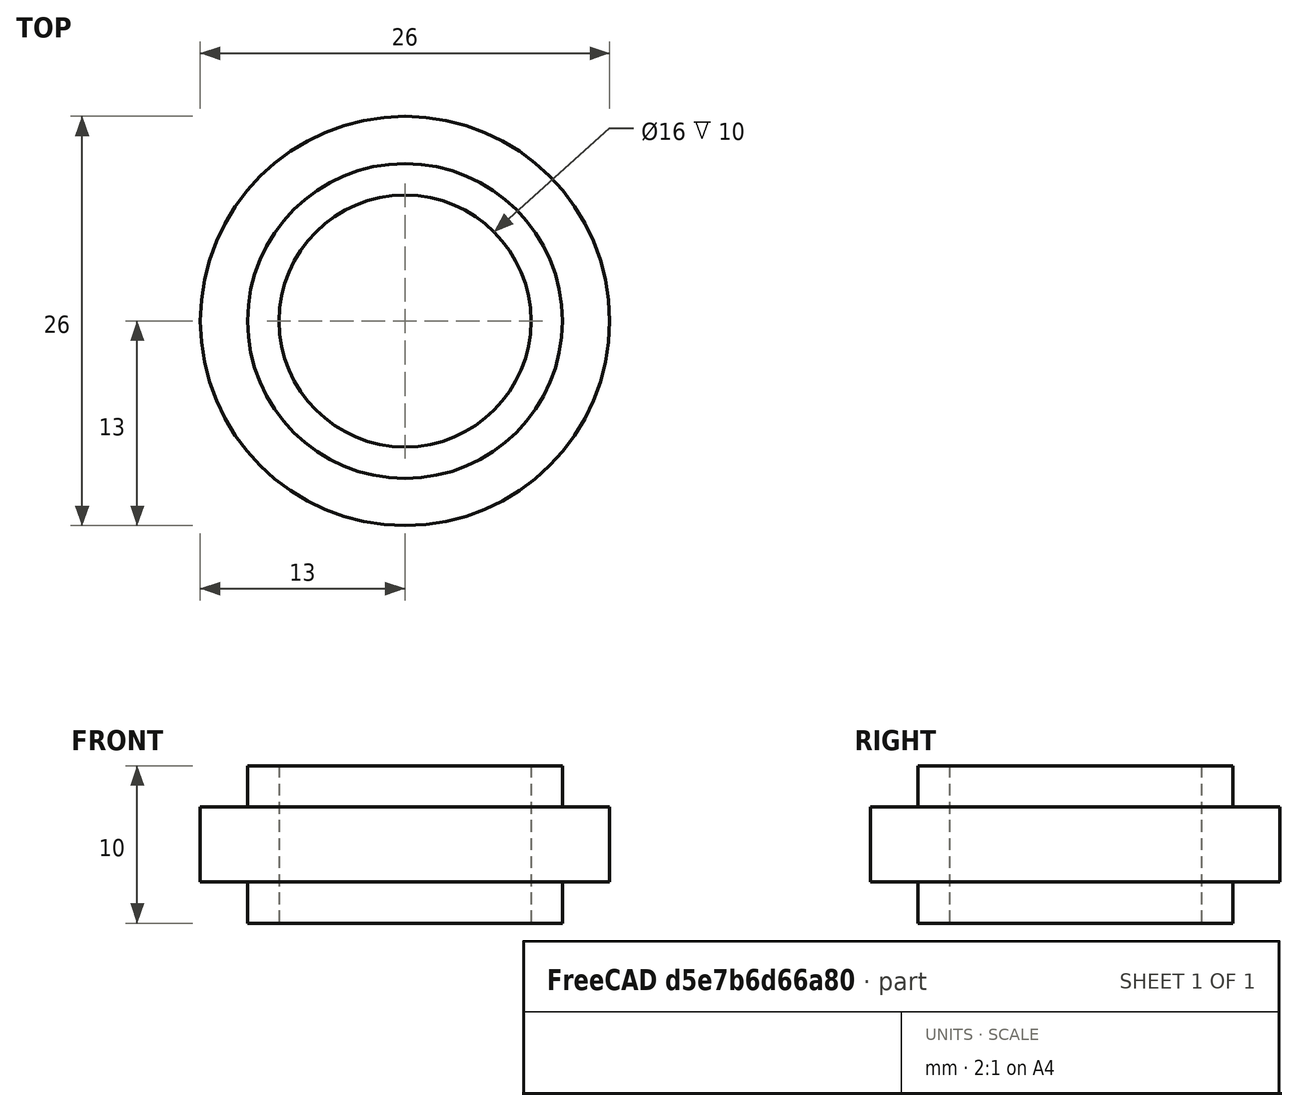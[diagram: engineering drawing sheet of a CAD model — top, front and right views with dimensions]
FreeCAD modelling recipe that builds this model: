
FCSTD DOCUMENT  (FreeCAD 0.19R)
Label: x-axis-roller
License: All rights reserved
LicenseURL: http://en.wikipedia.org/wiki/All_rights_reserved
objects: Sketcher::SketchObject×1, PartDesign::Revolution×1, PartDesign::Body×1
note: 4 computed .brp shape members not serialized (recipe doc carries the construction recipe); baked Part::Feature solids carry a one-line shape summary decoded from their .brp

FEATURE [Sketcher::SketchObject] Sketch
  FullyConstrained = true
  MapMode = 5
  Placement = pos=(0,0,0) rot=(1,0,0;1.5708rad)
  Support = -> [XZ_Plane]
  sketch-geometry (8):
    g0: LineSegment StartX=8 StartY=10 StartZ=0 EndX=8 EndY=0 EndZ=0
    g1: LineSegment StartX=8 StartY=10 StartZ=0 EndX=10 EndY=10 EndZ=0
    g2: LineSegment StartX=10 StartY=10 StartZ=0 EndX=10 EndY=7.375 EndZ=0
    g3: LineSegment StartX=10 StartY=7.375 StartZ=0 EndX=13 EndY=7.375 EndZ=0
    g4: LineSegment StartX=13 StartY=7.375 StartZ=0 EndX=13 EndY=2.625 EndZ=0
    g5: LineSegment StartX=13 StartY=2.625 StartZ=0 EndX=10 EndY=2.625 EndZ=0
    g6: LineSegment StartX=10 StartY=2.625 StartZ=0 EndX=10 EndY=0 EndZ=0
    g7: LineSegment StartX=10 StartY=0 StartZ=0 EndX=8 EndY=0 EndZ=0
  constraints (24):
    c: PointOnObject(g0,g-1)
    c: Vertical(g0)
    c: Coincident(g1,g0)
    c: Horizontal(g1)
    c: Coincident(g2,g1)
    c: Vertical(g2)
    c: Coincident(g3,g2)
    c: Horizontal(g3)
    c: Coincident(g4,g3)
    c: Vertical(g4)
    c: Coincident(g5,g4)
    c: Horizontal(g5)
    c: Coincident(g6,g5)
    c: PointOnObject(g6,g-1)
    c: Vertical(g6)
    c: Coincident(g7,g6)
    c: Coincident(g7,g0)
    c: Equal(g6,g2)
    c: Equal(g3,g5)
    c: DistanceY(g4,g4) = 4.75
    c: DistanceX(g-1,g0) = 8
    c: DistanceY(g0,g0) = 10
    c: DistanceX(g1,g1) = 2
    c: DistanceX(g3,g3) = 3
FEATURE [PartDesign::Revolution] Revolution
  Angle = 360
  Axis = (0,-2e-16,1)
  Base = (0,0,0)
  Placement = pos=(0,0,0) rot=(1,0,0;1.5708rad)
  Profile = -> Sketch
  ReferenceAxis = -> Sketch [V_Axis]
  Reversed = true
FEATURE [PartDesign::Body] Body
  Group = -> [Sketch,Revolution]
  Origin = -> Origin
  Tip = -> Revolution
